# Revit family: KNS_LM_LS_Поворот плавный LESTA_IEK
name_source: partatom
category: Соединительные детали кабельных лотков
units: mm (PartAtom-declared; Revit-internal decimal feet)

## family parameters
Всегда вертикально = Да
Заголовок OmniClass = Cable Trays and Horizontal Racks
На основе рабочей плоскости = Нет
Номер OmniClass = 23.80.30.17.17
Общий = Нет
При загрузке вырезать с полостями = Нет
Размер круглого соединителя = Использовать диаметр
Тип детали = Отвод ступенчатого

## types (4) — shared parameters
ADSK_Версия Revit = 2019
ADSK_Версия семейства = 1.3
ADSK_Группирование = Кабельные лотки и аксессуары
ADSK_Единица измерения = шт
ADSK_Завод-изготовитель = IEK
ADSK_Марка = LESTA
ETIM_Class code = EC000856
ETIM_Class version = 7
IEK_Гарантийный срок = 3 года
IEK_Срок службы = 20 лет
KSI_CMa_Строительные материалы = 10.3.02.06
KSI_CPr_Строительные изделия = CPr>CGKG090
URL = https://www.iek.ru
Изготовитель = IEK

## per-type parameters (varying)
| type | ADSK_Материал | ADSK_Наименование краткое | IEK_Поиск в таблице имен | Радиус поворота | Тип крышки | Тип перегородки |
| OS_R300 | IEK_Металл_OS | Поворот лестничный LESTA OS R300 IEK | KNS_LM_LS_Поворот плавный LESTA | 300 мм | KNS_LM_LS_Крышка поворота плавного LESTA_IEK : OS_R300 |  |
| OS_R600 | IEK_Металл_OS | Поворот лестничный LESTA OS R600 IEK | KNS_LM_LS_Поворот плавный LESTA | 600 мм | KNS_LM_LS_Крышка поворота плавного LESTA_IEK : OS_R600 | KNS_LM_LS_Крышка поворота плавного LESTA_IEK : OS_R300 |
| HDZ_R300 | IEK_Металл_HDZ | Поворот лестничный LESTA HDZ R300 IEK | KNS_LM_LS_Поворот плавный LESTA_HDZ | 300 мм | KNS_LM_LS_Крышка поворота плавного LESTA_IEK : HDZ_R300 | KNS_LM_LS_Крышка поворота плавного LESTA_IEK : OS_R300 |
| HDZ_R600 | IEK_Металл_HDZ | Поворот лестничный LESTA HDZ R600 IEK | KNS_LM_LS_Поворот плавный LESTA_HDZ | 600 мм | KNS_LM_LS_Крышка поворота плавного LESTA_IEK : HDZ_R600 | KNS_LM_LS_Крышка поворота плавного LESTA_IEK : OS_R300 |
